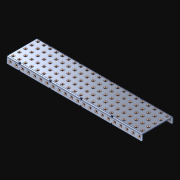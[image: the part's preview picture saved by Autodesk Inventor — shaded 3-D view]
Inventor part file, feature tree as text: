
AUTODESK INVENTOR PART (.ipt)
format: ipt  version: 2021 (Build 250183000, 183)  size: 2,052,608 bytes
history: native  units: in
note: dims shown in document units (in); Inventor stores cm internally (conversion verified against a paired STEP export)
features: extrude x155, other x155, sketch x4, pattern_linear x3
ambient origin geometry x8: Origin, YZ Plane, XZ Plane, XY Plane, X Axis, Y Axis, Z Axis, Center Point
bodies: Solid1 (feature_tree)
feature tree (317):
  pattern_linear  "Rectangular Pattern1"  Spacing1=0.182in  [1 undecoded]
  pattern_linear  "Rectangular Pattern2"  Spacing1=0.046in  [1 undecoded]
  pattern_linear  "Rectangular Pattern3"  Spacing1=0.5in  [1 undecoded]
  extrude  "Extrusion1"  Depth=0.046in
  sketch  "Sketch1"  dims[d0=0.182in]
  other  "Srf1"
  sketch  "Sketch2"  dims[d1=0.046in d2=0.0in]
  other  "Srf2"
  sketch  "Sketch3"  dims[d3=0.182in]
  other  "Srf3"
  other  "Srf4"
  other  "Srf5"
  other  "Srf6"
  other  "Srf7"
  other  "Srf8"
  other  "Srf9"
  other  "Srf10"
  other  "Srf11"
  other  "Srf12"
  other  "Srf13"
  other  "Srf14"
  other  "Srf15"
  other  "Srf16"
  other  "Srf17"
  other  "Srf18"
  other  "Srf19"
  other  "Srf20"
  other  "Srf21"
  other  "Srf22"
  other  "Srf23"
  other  "Srf24"
  other  "Srf38"
  other  "Srf39"
  other  "Srf40"
  other  "Srf41"
  other  "Srf42"
  other  "Srf43"
  other  "Srf44"
  other  "Srf45"
  other  "Srf46"
  other  "Srf47"
  other  "Srf48"
  other  "Srf49"
  other  "Srf50"
  other  "Srf51"
  other  "Srf52"
  other  "Srf53"
  other  "Srf54"
  other  "Srf55"
  other  "Srf56"
  other  "Srf57"
  other  "Srf58"
  other  "Srf72"
  other  "Srf73"
  other  "Srf74"
  other  "Srf75"
  other  "Srf76"
  other  "Srf77"
  other  "Srf78"
  other  "Srf79"
  other  "Srf80"
  other  "Srf81"
  other  "Srf82"
  other  "Srf83"
  other  "Srf84"
  other  "Srf85"
  other  "Srf86"
  other  "Srf87"
  other  "Srf88"
  other  "Srf89"
  other  "Srf90"
  other  "Srf91"
  other  "Srf92"
  other  "Srf93"
  other  "Srf107"
  other  "Srf108"
  other  "Srf109"
  other  "Srf110"
  other  "Srf111"
  other  "Srf112"
  other  "Srf113"
  other  "Srf114"
  other  "Srf115"
  other  "Srf116"
  other  "Srf117"
  other  "Srf118"
  other  "Srf119"
  other  "Srf120"
  other  "Srf121"
  other  "Srf122"
  other  "Srf123"
  other  "Srf124"
  other  "Srf125"
  other  "Srf126"
  other  "Srf127"
  other  "Srf128"
  other  "Srf142"
  other  "Srf143"
  other  "Srf144"
  other  "Srf145"
  other  "Srf146"
  other  "Srf147"
  other  "Srf148"
  other  "Srf149"
  other  "Srf150"
  other  "Srf151"
  other  "Srf152"
  other  "Srf153"
  other  "Srf154"
  other  "Srf155"
  other  "Srf156"
  other  "Srf157"
  other  "Srf158"
  other  "Srf159"
  other  "Srf160"
  other  "Srf161"
  other  "Srf162"
  other  "Srf163"
  other  "Srf177"
  other  "Srf178"
  other  "Srf179"
  other  "Srf180"
  other  "Srf181"
  other  "Srf182"
  other  "Srf183"
  other  "Srf184"
  other  "Srf185"
  other  "Srf186"
  other  "Srf187"
  other  "Srf188"
  other  "Srf189"
  other  "Srf190"
  other  "Srf191"
  other  "Srf192"
  other  "Srf193"
  other  "Srf194"
  other  "Srf195"
  other  "Srf196"
  other  "Srf197"
  other  "Srf198"
  other  "Srf212"
  other  "Srf213"
  other  "Srf214"
  other  "Srf215"
  other  "Srf216"
  other  "Srf217"
  other  "Srf218"
  other  "Srf219"
  other  "Srf220"
  other  "Srf221"
  other  "Srf222"
  other  "Srf223"
  other  "Srf224"
  other  "Srf225"
  other  "Srf226"
  other  "Srf227"
  other  "Srf228"
  other  "Srf229"
  other  "Srf230"
  other  "Srf231"
  other  "Srf232"
  sketch  "Sketch4"  dims[d4=0.046in d5=0.0in d6=0.182in d7=0.046in d8=0.0in d11=0.5in d12=8.6614in d14=0.5in d15=1.9685in d17=0.5in d18=8.6614in d20=0.5in d21=6.5in d22=0.0in]
  parser-record x1  (decoder bookkeeping rows leaked as tree rows — omitted from the tree; the rows remain in map.json)
  extrude  "ExtrusionSrf1"  Depth=0.046in
  extrude  "ExtrusionSrf2"  Depth=0.046in
  extrude  "ExtrusionSrf3"  Depth=0.046in
  extrude  "ExtrusionSrf4"  Depth=0.046in
  extrude  "ExtrusionSrf5"  Depth=0.046in
  extrude  "ExtrusionSrf6"  TaperAngle=0.0deg  [1 undecoded]
  extrude  "ExtrusionSrf7"  [1 undecoded]
  extrude  "ExtrusionSrf8"  [1 undecoded]
  extrude  "ExtrusionSrf9"  [1 undecoded]
  extrude  "ExtrusionSrf10"  [1 undecoded]
  extrude  "ExtrusionSrf11"  [1 undecoded]
  extrude  "ExtrusionSrf12"  [1 undecoded]
  extrude  "ExtrusionSrf13"  [1 undecoded]
  extrude  "ExtrusionSrf14"  [1 undecoded]
  extrude  "ExtrusionSrf15"  [1 undecoded]
  extrude  "ExtrusionSrf16"  [1 undecoded]
  extrude  "ExtrusionSrf17"  [1 undecoded]
  extrude  "ExtrusionSrf18"  [1 undecoded]
  extrude  "ExtrusionSrf19"  [1 undecoded]
  extrude  "ExtrusionSrf20"  [1 undecoded]
  extrude  "ExtrusionSrf21"  [1 undecoded]
  extrude  "ExtrusionSrf22"  [1 undecoded]
  extrude  "ExtrusionSrf23"  [1 undecoded]
  extrude  "ExtrusionSrf24"  [1 undecoded]
  extrude  "ExtrusionSrf38"  [1 undecoded]
  extrude  "ExtrusionSrf39"  [1 undecoded]
  extrude  "ExtrusionSrf40"  [1 undecoded]
  extrude  "ExtrusionSrf41"  [1 undecoded]
  extrude  "ExtrusionSrf42"  [1 undecoded]
  extrude  "ExtrusionSrf43"  [1 undecoded]
  extrude  "ExtrusionSrf44"  [1 undecoded]
  extrude  "ExtrusionSrf45"  [1 undecoded]
  extrude  "ExtrusionSrf46"  [1 undecoded]
  extrude  "ExtrusionSrf47"  [1 undecoded]
  extrude  "ExtrusionSrf48"  [1 undecoded]
  extrude  "ExtrusionSrf49"  [1 undecoded]
  extrude  "ExtrusionSrf50"  [1 undecoded]
  extrude  "ExtrusionSrf51"  [1 undecoded]
  extrude  "ExtrusionSrf52"  [1 undecoded]
  extrude  "ExtrusionSrf53"  [1 undecoded]
  extrude  "ExtrusionSrf54"  [1 undecoded]
  extrude  "ExtrusionSrf55"  [1 undecoded]
  extrude  "ExtrusionSrf56"  [1 undecoded]
  extrude  "ExtrusionSrf57"  [1 undecoded]
  extrude  "ExtrusionSrf58"  [1 undecoded]
  extrude  "ExtrusionSrf72"  [1 undecoded]
  extrude  "ExtrusionSrf73"  [1 undecoded]
  extrude  "ExtrusionSrf74"  [1 undecoded]
  extrude  "ExtrusionSrf75"  [1 undecoded]
  extrude  "ExtrusionSrf76"  [1 undecoded]
  extrude  "ExtrusionSrf77"  [1 undecoded]
  extrude  "ExtrusionSrf78"  [1 undecoded]
  extrude  "ExtrusionSrf79"  [1 undecoded]
  extrude  "ExtrusionSrf80"  [1 undecoded]
  extrude  "ExtrusionSrf81"  [1 undecoded]
  extrude  "ExtrusionSrf82"  [1 undecoded]
  extrude  "ExtrusionSrf83"  [1 undecoded]
  extrude  "ExtrusionSrf84"  [1 undecoded]
  extrude  "ExtrusionSrf85"  [1 undecoded]
  extrude  "ExtrusionSrf86"  [1 undecoded]
  extrude  "ExtrusionSrf87"  [1 undecoded]
  extrude  "ExtrusionSrf88"  [1 undecoded]
  extrude  "ExtrusionSrf89"  [1 undecoded]
  extrude  "ExtrusionSrf90"  [1 undecoded]
  extrude  "ExtrusionSrf91"  [1 undecoded]
  extrude  "ExtrusionSrf92"  [1 undecoded]
  extrude  "ExtrusionSrf93"  [1 undecoded]
  extrude  "ExtrusionSrf107"  [1 undecoded]
  extrude  "ExtrusionSrf108"  [1 undecoded]
  extrude  "ExtrusionSrf109"  [1 undecoded]
  extrude  "ExtrusionSrf110"  [1 undecoded]
  extrude  "ExtrusionSrf111"  [1 undecoded]
  extrude  "ExtrusionSrf112"  [1 undecoded]
  extrude  "ExtrusionSrf113"  [1 undecoded]
  extrude  "ExtrusionSrf114"  [1 undecoded]
  extrude  "ExtrusionSrf115"  [1 undecoded]
  extrude  "ExtrusionSrf116"  [1 undecoded]
  extrude  "ExtrusionSrf117"  [1 undecoded]
  extrude  "ExtrusionSrf118"  [1 undecoded]
  extrude  "ExtrusionSrf119"  [1 undecoded]
  extrude  "ExtrusionSrf120"  [1 undecoded]
  extrude  "ExtrusionSrf121"  [1 undecoded]
  extrude  "ExtrusionSrf122"  [1 undecoded]
  extrude  "ExtrusionSrf123"  [1 undecoded]
  extrude  "ExtrusionSrf124"  [1 undecoded]
  extrude  "ExtrusionSrf125"  [1 undecoded]
  extrude  "ExtrusionSrf126"  [1 undecoded]
  extrude  "ExtrusionSrf127"  [1 undecoded]
  extrude  "ExtrusionSrf128"  [1 undecoded]
  extrude  "ExtrusionSrf142"  [1 undecoded]
  extrude  "ExtrusionSrf143"  [1 undecoded]
  extrude  "ExtrusionSrf144"  [1 undecoded]
  extrude  "ExtrusionSrf145"  [1 undecoded]
  extrude  "ExtrusionSrf146"  [1 undecoded]
  extrude  "ExtrusionSrf147"  [1 undecoded]
  extrude  "ExtrusionSrf148"  [1 undecoded]
  extrude  "ExtrusionSrf149"  [1 undecoded]
  extrude  "ExtrusionSrf150"  [1 undecoded]
  extrude  "ExtrusionSrf151"  [1 undecoded]
  extrude  "ExtrusionSrf152"  [1 undecoded]
  extrude  "ExtrusionSrf153"  [1 undecoded]
  extrude  "ExtrusionSrf154"  [1 undecoded]
  extrude  "ExtrusionSrf155"  [1 undecoded]
  extrude  "ExtrusionSrf156"  [1 undecoded]
  extrude  "ExtrusionSrf157"  [1 undecoded]
  extrude  "ExtrusionSrf158"  [1 undecoded]
  extrude  "ExtrusionSrf159"  [1 undecoded]
  extrude  "ExtrusionSrf160"  [1 undecoded]
  extrude  "ExtrusionSrf161"  [1 undecoded]
  extrude  "ExtrusionSrf162"  [1 undecoded]
  extrude  "ExtrusionSrf163"  [1 undecoded]
  extrude  "ExtrusionSrf177"  [1 undecoded]
  extrude  "ExtrusionSrf178"  [1 undecoded]
  extrude  "ExtrusionSrf179"  [1 undecoded]
  extrude  "ExtrusionSrf180"  [1 undecoded]
  extrude  "ExtrusionSrf181"  [1 undecoded]
  extrude  "ExtrusionSrf182"  [1 undecoded]
  extrude  "ExtrusionSrf183"  [1 undecoded]
  extrude  "ExtrusionSrf184"  [1 undecoded]
  extrude  "ExtrusionSrf185"  [1 undecoded]
  extrude  "ExtrusionSrf186"  [1 undecoded]
  extrude  "ExtrusionSrf187"  [1 undecoded]
  extrude  "ExtrusionSrf188"  [1 undecoded]
  extrude  "ExtrusionSrf189"  [1 undecoded]
  extrude  "ExtrusionSrf190"  [1 undecoded]
  extrude  "ExtrusionSrf191"  [1 undecoded]
  extrude  "ExtrusionSrf192"  [1 undecoded]
  extrude  "ExtrusionSrf193"  [1 undecoded]
  extrude  "ExtrusionSrf194"  [1 undecoded]
  extrude  "ExtrusionSrf195"  [1 undecoded]
  extrude  "ExtrusionSrf196"  [1 undecoded]
  extrude  "ExtrusionSrf197"  [1 undecoded]
  extrude  "ExtrusionSrf198"  [1 undecoded]
  extrude  "ExtrusionSrf212"  [1 undecoded]
  extrude  "ExtrusionSrf213"  [1 undecoded]
  extrude  "ExtrusionSrf214"  [1 undecoded]
  extrude  "ExtrusionSrf215"  [1 undecoded]
  extrude  "ExtrusionSrf216"  [1 undecoded]
  extrude  "ExtrusionSrf217"  [1 undecoded]
  extrude  "ExtrusionSrf218"  [1 undecoded]
  extrude  "ExtrusionSrf219"  [1 undecoded]
  extrude  "ExtrusionSrf220"  [1 undecoded]
  extrude  "ExtrusionSrf221"  [1 undecoded]
  extrude  "ExtrusionSrf222"  [1 undecoded]
  extrude  "ExtrusionSrf223"  [1 undecoded]
  extrude  "ExtrusionSrf224"  [1 undecoded]
  extrude  "ExtrusionSrf225"  [1 undecoded]
  extrude  "ExtrusionSrf226"  [1 undecoded]
  extrude  "ExtrusionSrf227"  [1 undecoded]
  extrude  "ExtrusionSrf228"  [1 undecoded]
  extrude  "ExtrusionSrf229"  [1 undecoded]
  extrude  "ExtrusionSrf230"  [1 undecoded]
  extrude  "ExtrusionSrf231"  [1 undecoded]
  extrude  "ExtrusionSrf232"  [1 undecoded]
note: 152 required parameter values undecoded (feature->parameter linkage not recoverable at this tier; creation-order binding heuristic only, values carry confidence <= 0.55)
